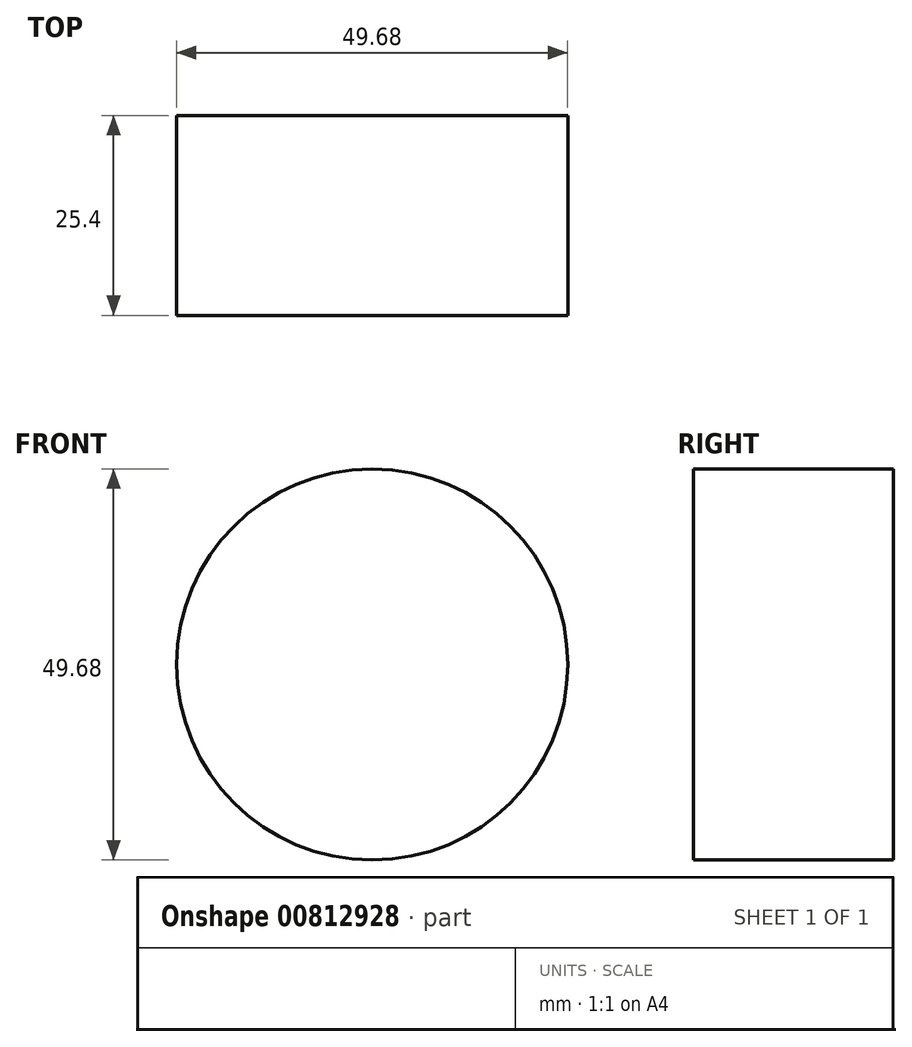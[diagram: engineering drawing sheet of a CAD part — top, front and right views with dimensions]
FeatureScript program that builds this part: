
annotation { "Feature Type Name" : "Feature", "Feature Type Description" : "" }
export const myFeature = defineFeature(function(context is Context, id is Id, definition is map)
    precondition{}
    {
        {
            var Q0;
            Q0=qCreatedBy(makeId("Front.planeOp"),FACE);
            var sketch = newSketch(context, id + "F0", { "sketchPlane" : qUnion([Q0])});
            skCircle(sketch, "E0", {"center": v(-6.35, 17.2) * mm, "radius": 24.84 * mm});
            skSolve(sketch);
        }
        {
            var Q0;
            Q0=sQuery(id+"F0.wireOp",EDGE,"E0");
            extrude(context, id + "F1", {"bodyType" : ToolBodyType.SURFACE, "surfaceEntities" : qUnion([Q0]), "endBound" : BoundingType.SYMMETRIC, "depth" : 25.4 * mm, "offsetDistance" : 25.4 * mm});
        }
    });
